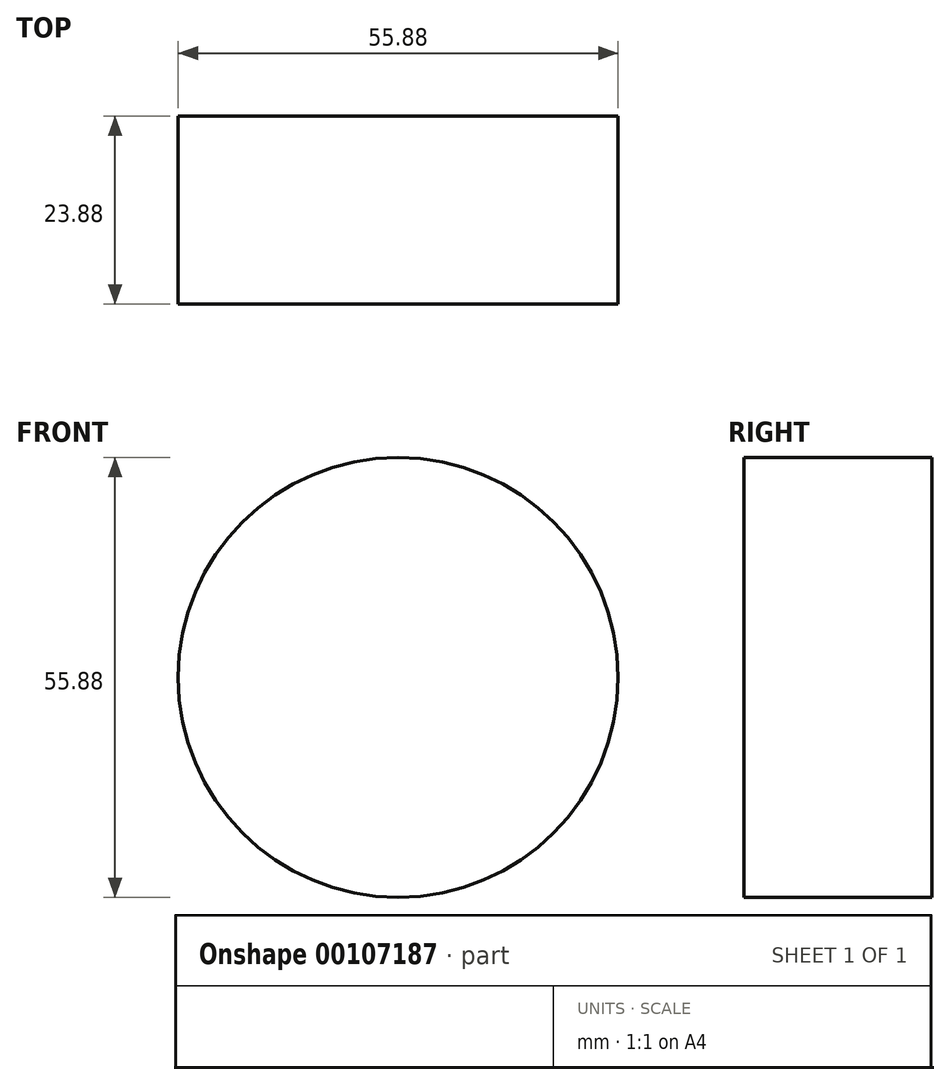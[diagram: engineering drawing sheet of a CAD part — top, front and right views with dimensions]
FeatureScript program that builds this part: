
annotation { "Feature Type Name" : "Feature", "Feature Type Description" : "" }
export const myFeature = defineFeature(function(context is Context, id is Id, definition is map)
    precondition{}
    {
        {
            var Q0;
            Q0=qCreatedBy(makeId("Front.planeOp"),FACE);
            var sketch = newSketch(context, id + "F0", { "sketchPlane" : qUnion([Q0])});
            skCircle(sketch, "E0", {"center": v(0, 0) * mm, "radius": 27.94 * mm});
            skSolve(sketch);
        }
        {
            var Q0;
            Q0=makeQuery(id+"F0.imprint","IMPRINT",FACE,{"disambiguationData":[TD([[makeQuery(id+"F0.imprint","IMPRINT",EDGE,{"derivedFrom":sQuery(id+"F0.wireOp",EDGE,"E0")}),1.0]])]});
            extrude(context, id + "F1", {"entities" : qUnion([Q0]), "depth" : 23.88 * mm});
        }
    });
